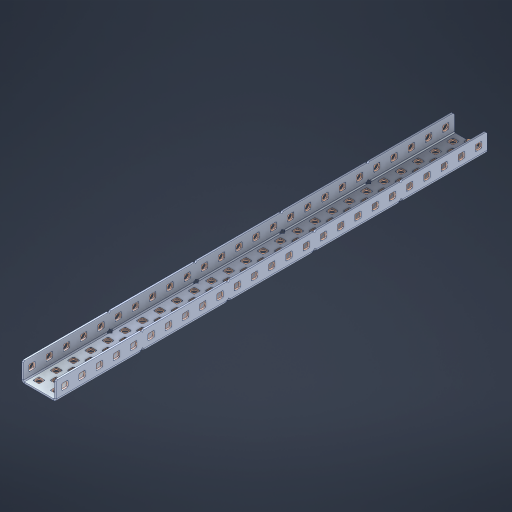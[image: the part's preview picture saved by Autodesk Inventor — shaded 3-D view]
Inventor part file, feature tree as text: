
AUTODESK INVENTOR PART (.ipt)
format: ipt  version: 2023 (Build 270158000, 158)  size: 1,628,160 bytes
history: native  units: in
note: dims shown in document units (in); Inventor stores cm internally (conversion verified against a paired STEP export)
features: other x132, extrude x123, sheet_metal_op x11, sketch x10, pattern_linear x2, mirror x1, chamfer x1
ambient origin geometry x8: Origin, YZ Plane, XZ Plane, XY Plane, X Axis, Y Axis, Z Axis, Center Point
bodies: Solid1 (feature_tree), Body (feature_tree)
feature tree (280):
  sheet_metal_op  "Flanges"
  other  "Flange Pattern Plane"
  other  "Flange Pattern Sketch"
  sheet_metal_op  "Flange Pattern"
  sheet_metal_op  "Body Pattern"
  pattern_linear  "Center Pattern"  Spacing1=0.0469in  [1 undecoded]
  other  "Arc Length"
  mirror  "Notch Mirror"
  pattern_linear  "Notch Pattern"  Spacing1=0.182in  [1 undecoded]
  chamfer  "End Chamfer"
  extrude  "Half Cut"  Depth=0.02in
  sketch  "Sketch1"  dims[d0=1.0in]
  other  "Plate1"
  sketch  "Sketch2"  dims[d1=12.5in]
  other  "Plate2"
  sheet_metal_op  "Bend1"
  sheet_metal_op  "Corner1"
  sketch  "Sketch3"  dims[d2=0.0469in]
  sketch  "Sketch7"  dims[d3=0.0469in]
  other  "Srf1"
  other  "Srf2"
  sketch  "Sketch8"  dims[d4=0.0234in]
  sketch  "Sketch9"  dims[d5=0.0938in]
  other  "Srf91"
  sheet_metal_op  "Body Pattern Sketch"
  other  "Srf92"
  sketch  "Sketch13"  dims[d6=0.0469in]
  sketch  "Sketch14"  dims[d7=0.5in d8=90.0deg d9=0.0312in]
  sketch  "Sketch15"  dims[d10=0.1875in]
  sketch  "Sketch16"  dims[d11=0.0469in d12=0.0469in d16=0.182in d17=0.02in d18=0.0469in d19=0.0in d20=0.25in d21=0.25in d38=9.8425in d40=0.5in d41=0.7874in d43=1.0in d46=0.172in d47=1.0in d48=0.0in d49=0.182in d50=0.02in d51=0.25in d52=0.25in d53=0.0469in d54=0.0in d55=0.172in d56=1.0in d57=0.0in d58=0.25in d60=9.8425in d62=0.5in d63=0.7874in d65=0.5in d85=0.1227in d86=0.1659in d88=0.04in d89=0.0469in d90=0.0in d91=0.04in d92=0.0491in d95=2.5in d96=0.04in d97=0.25in d98=45.0deg d99=0.25in d100=0.5in d101=0.0in d102=2.497in d106=0.182in d107=0.02in d108=0.5in d109=0.5in d110=0.0469in d111=0.0in d112=0.172in d113=0.5in d114=0.0in d117=0.5in d118=0.5in d119=0.5in]
  other  "Srf786"
  other  "Srf823"
  other  "Srf824"
  other  "Srf825"
  other  "Srf826"
  other  "Srf827"
  other  "Srf828"
  other  "Srf829"
  other  "Srf856"
  other  "Srf857"
  other  "Srf858"
  other  "Srf859"
  other  "Srf860"
  other  "Srf861"
  other  "Srf862"
  other  "Srf889"
  other  "Srf890"
  other  "Srf891"
  other  "Srf892"
  other  "Srf893"
  other  "Srf894"
  other  "Srf895"
  other  "Srf896"
  other  "Srf922"
  other  "Srf923"
  other  "Srf924"
  other  "Srf925"
  other  "Srf926"
  other  "Srf959"
  other  "Srf960"
  other  "Srf961"
  other  "Srf962"
  other  "Srf963"
  other  "Srf996"
  other  "Srf997"
  other  "Srf998"
  other  "Srf999"
  other  "Srf1000"
  other  "Srf1143"
  other  "Srf1144"
  other  "Srf1145"
  other  "Srf1146"
  other  "Srf1147"
  other  "Srf1148"
  other  "Srf1149"
  other  "Srf1150"
  other  "Srf1151"
  other  "Srf1152"
  other  "Srf1153"
  other  "Srf1154"
  other  "Srf1155"
  other  "Srf1156"
  other  "Srf1157"
  other  "Srf1158"
  other  "Srf1159"
  other  "Srf1160"
  other  "Srf1161"
  other  "Srf1162"
  other  "Srf1163"
  other  "Srf1164"
  other  "Srf1165"
  other  "Srf1166"
  other  "Srf1167"
  other  "Srf1168"
  other  "Srf1169"
  other  "Srf1170"
  other  "Srf1171"
  other  "Srf1172"
  other  "Srf1173"
  other  "Srf1174"
  other  "Srf1175"
  other  "Srf1176"
  other  "Srf1177"
  other  "Srf1178"
  other  "Srf1199"
  other  "Srf1200"
  other  "Srf1201"
  other  "Srf1202"
  other  "Srf1203"
  other  "Srf1204"
  other  "Srf1205"
  other  "Srf1206"
  other  "Srf1207"
  other  "Srf1208"
  other  "Srf1209"
  other  "Srf1210"
  other  "Srf1211"
  other  "Srf1212"
  other  "Srf1213"
  other  "Srf1214"
  other  "Srf1215"
  other  "Srf1216"
  other  "Srf1217"
  other  "Srf1218"
  other  "Srf1219"
  other  "Srf1220"
  other  "Srf1221"
  other  "Srf1222"
  other  "Srf1223"
  other  "Srf1224"
  other  "Srf1225"
  other  "Srf1226"
  other  "Srf1227"
  other  "Srf1228"
  other  "Srf1229"
  other  "Srf1230"
  other  "Srf1231"
  other  "Srf1232"
  other  "Srf1233"
  other  "Srf1234"
  other  "Srf1255"
  other  "Srf1256"
  other  "Srf1257"
  other  "Srf1258"
  other  "Srf1259"
  other  "Srf1260"
  other  "Srf1261"
  other  "Srf1262"
  other  "Srf1263"
  other  "Srf1264"
  other  "Srf1265"
  sheet_metal_op  "Flange Stamp"
  sheet_metal_op  "Flange Circle"
  sheet_metal_op  "Body Stamp"
  sheet_metal_op  "Body Circle"
  other  "Center Stamp"
  other  "Center Circle"
  sheet_metal_op  "Notch"
  extrude  "ExtrusionSrf2"  Depth=0.0469in
  extrude  "ExtrusionSrf92"  TaperAngle=0.0deg  [1 undecoded]
  extrude  "ExtrusionSrf823"  Depth=0.5in
  extrude  "ExtrusionSrf824"  Depth=0.5in
  extrude  "ExtrusionSrf825"  Depth=0.5in
  extrude  "ExtrusionSrf826"  Depth=0.5in
  extrude  "ExtrusionSrf827"  Depth=1.0in TaperAngle=0.0deg
  extrude  "ExtrusionSrf828"  Depth=0.5in
  extrude  "ExtrusionSrf829"  Depth=0.02in
  extrude  "ExtrusionSrf856"  Depth=0.5in
  extrude  "ExtrusionSrf857"  Depth=0.5in
  extrude  "ExtrusionSrf858"  Depth=0.0469in
  extrude  "ExtrusionSrf859"  TaperAngle=0.0deg  [1 undecoded]
  extrude  "ExtrusionSrf860"  Depth=0.5in
  extrude  "ExtrusionSrf861"  Depth=1.0in TaperAngle=0.0deg
  extrude  "ExtrusionSrf862"  Depth=0.5in
  extrude  "ExtrusionSrf889"  Depth=0.5in
  extrude  "ExtrusionSrf890"  Depth=0.5in
  extrude  "ExtrusionSrf891"  Depth=0.5in
  extrude  "ExtrusionSrf892"  Depth=0.5in
  extrude  "ExtrusionSrf893"  Depth=0.5in
  extrude  "ExtrusionSrf894"  Depth=0.0469in
  extrude  "ExtrusionSrf895"  TaperAngle=0.0deg  [1 undecoded]
  extrude  "ExtrusionSrf896"  Depth=0.5in
  extrude  "ExtrusionSrf922"  Depth=0.5in
  extrude  "ExtrusionSrf923"  Depth=2.5in
  extrude  "ExtrusionSrf924"  Depth=0.5in TaperAngle=45.0deg
  extrude  "ExtrusionSrf925"  Depth=0.5in
  extrude  "ExtrusionSrf926"  Depth=0.5in TaperAngle=0.0deg
  extrude  "ExtrusionSrf959"  Depth=0.5in
  extrude  "ExtrusionSrf960"  Depth=0.5in
  extrude  "ExtrusionSrf961"  Depth=0.02in
  extrude  "ExtrusionSrf962"  Depth=0.5in
  extrude  "ExtrusionSrf963"  Depth=0.5in
  extrude  "ExtrusionSrf996"  Depth=0.0469in
  extrude  "ExtrusionSrf997"  TaperAngle=0.0deg  [1 undecoded]
  extrude  "ExtrusionSrf998"  Depth=0.5in
  extrude  "ExtrusionSrf999"  Depth=0.5in TaperAngle=0.0deg
  extrude  "ExtrusionSrf1000"  Depth=0.5in
  extrude  "ExtrusionSrf1143"  Depth=0.5in
  extrude  "ExtrusionSrf1144"  Depth=0.5in
  extrude  "ExtrusionSrf1145"  [1 undecoded]
  extrude  "ExtrusionSrf1146"  [1 undecoded]
  extrude  "ExtrusionSrf1147"  [1 undecoded]
  extrude  "ExtrusionSrf1148"  [1 undecoded]
  extrude  "ExtrusionSrf1149"  [1 undecoded]
  extrude  "ExtrusionSrf1150"  [1 undecoded]
  extrude  "ExtrusionSrf1151"  [1 undecoded]
  extrude  "ExtrusionSrf1152"  [1 undecoded]
  extrude  "ExtrusionSrf1153"  [1 undecoded]
  extrude  "ExtrusionSrf1154"  [1 undecoded]
  extrude  "ExtrusionSrf1155"  [1 undecoded]
  extrude  "ExtrusionSrf1156"  [1 undecoded]
  extrude  "ExtrusionSrf1157"  [1 undecoded]
  extrude  "ExtrusionSrf1158"  [1 undecoded]
  extrude  "ExtrusionSrf1159"  [1 undecoded]
  extrude  "ExtrusionSrf1160"  [1 undecoded]
  extrude  "ExtrusionSrf1161"  [1 undecoded]
  extrude  "ExtrusionSrf1162"  [1 undecoded]
  extrude  "ExtrusionSrf1163"  [1 undecoded]
  extrude  "ExtrusionSrf1164"  [1 undecoded]
  extrude  "ExtrusionSrf1165"  [1 undecoded]
  extrude  "ExtrusionSrf1166"  [1 undecoded]
  extrude  "ExtrusionSrf1167"  [1 undecoded]
  extrude  "ExtrusionSrf1168"  [1 undecoded]
  extrude  "ExtrusionSrf1169"  [1 undecoded]
  extrude  "ExtrusionSrf1170"  [1 undecoded]
  extrude  "ExtrusionSrf1171"  [1 undecoded]
  extrude  "ExtrusionSrf1172"  [1 undecoded]
  extrude  "ExtrusionSrf1173"  [1 undecoded]
  extrude  "ExtrusionSrf1174"  [1 undecoded]
  extrude  "ExtrusionSrf1175"  [1 undecoded]
  extrude  "ExtrusionSrf1176"  [1 undecoded]
  extrude  "ExtrusionSrf1177"  [1 undecoded]
  extrude  "ExtrusionSrf1178"  [1 undecoded]
  extrude  "ExtrusionSrf1199"  [1 undecoded]
  extrude  "ExtrusionSrf1200"  [1 undecoded]
  extrude  "ExtrusionSrf1201"  [1 undecoded]
  extrude  "ExtrusionSrf1202"  [1 undecoded]
  extrude  "ExtrusionSrf1203"  [1 undecoded]
  extrude  "ExtrusionSrf1204"  [1 undecoded]
  extrude  "ExtrusionSrf1205"  [1 undecoded]
  extrude  "ExtrusionSrf1206"  [1 undecoded]
  extrude  "ExtrusionSrf1207"  [1 undecoded]
  extrude  "ExtrusionSrf1208"  [1 undecoded]
  extrude  "ExtrusionSrf1209"  [1 undecoded]
  extrude  "ExtrusionSrf1210"  [1 undecoded]
  extrude  "ExtrusionSrf1211"  [1 undecoded]
  extrude  "ExtrusionSrf1212"  [1 undecoded]
  extrude  "ExtrusionSrf1213"  [1 undecoded]
  extrude  "ExtrusionSrf1214"  [1 undecoded]
  extrude  "ExtrusionSrf1215"  [1 undecoded]
  extrude  "ExtrusionSrf1216"  [1 undecoded]
  extrude  "ExtrusionSrf1217"  [1 undecoded]
  extrude  "ExtrusionSrf1218"  [1 undecoded]
  extrude  "ExtrusionSrf1219"  [1 undecoded]
  extrude  "ExtrusionSrf1220"  [1 undecoded]
  extrude  "ExtrusionSrf1221"  [1 undecoded]
  extrude  "ExtrusionSrf1222"  [1 undecoded]
  extrude  "ExtrusionSrf1223"  [1 undecoded]
  extrude  "ExtrusionSrf1224"  [1 undecoded]
  extrude  "ExtrusionSrf1225"  [1 undecoded]
  extrude  "ExtrusionSrf1226"  [1 undecoded]
  extrude  "ExtrusionSrf1227"  [1 undecoded]
  extrude  "ExtrusionSrf1228"  [1 undecoded]
  extrude  "ExtrusionSrf1229"  [1 undecoded]
  extrude  "ExtrusionSrf1230"  [1 undecoded]
  extrude  "ExtrusionSrf1231"  [1 undecoded]
  extrude  "ExtrusionSrf1232"  [1 undecoded]
  extrude  "ExtrusionSrf1233"  [1 undecoded]
  extrude  "ExtrusionSrf1234"  [1 undecoded]
  extrude  "ExtrusionSrf1255"  [1 undecoded]
  extrude  "ExtrusionSrf1256"  [1 undecoded]
  extrude  "ExtrusionSrf1257"  [1 undecoded]
  extrude  "ExtrusionSrf1258"  [1 undecoded]
  extrude  "ExtrusionSrf1259"  [1 undecoded]
  extrude  "ExtrusionSrf1260"  [1 undecoded]
  extrude  "ExtrusionSrf1261"  [1 undecoded]
  extrude  "ExtrusionSrf1262"  [1 undecoded]
  extrude  "ExtrusionSrf1263"  [1 undecoded]
  extrude  "ExtrusionSrf1264"  [1 undecoded]
  extrude  "ExtrusionSrf1265"  [1 undecoded]
note: 87 required parameter values undecoded (feature->parameter linkage not recoverable at this tier; creation-order binding heuristic only, values carry confidence <= 0.55)
